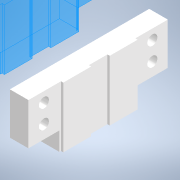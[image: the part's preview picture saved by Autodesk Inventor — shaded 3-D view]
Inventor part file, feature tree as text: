
AUTODESK INVENTOR PART (.ipt)
format: ipt  version: 2020 (Build 240168000, 168)  size: 178,176 bytes
history: native  units: mm
features: extrude x3, sketch x2, other x1
ambient origin geometry x8: Origin, YZ Plane, XZ Plane, XY Plane, X Axis, Y Axis, Z Axis, Center Point
bodies: Body1 (feature_tree)
feature tree (6):
  other  "Bryła1"
  extrude  "Wyciągnięcie proste1"  Depth=90.0mm
  sketch  "Szkic2"
  extrude  "Wyciągnięcie proste2"  Depth=12.0mm
  extrude  "Wyciągnięcie proste3"  Depth=45.0mm
  sketch  "Szkic1"
